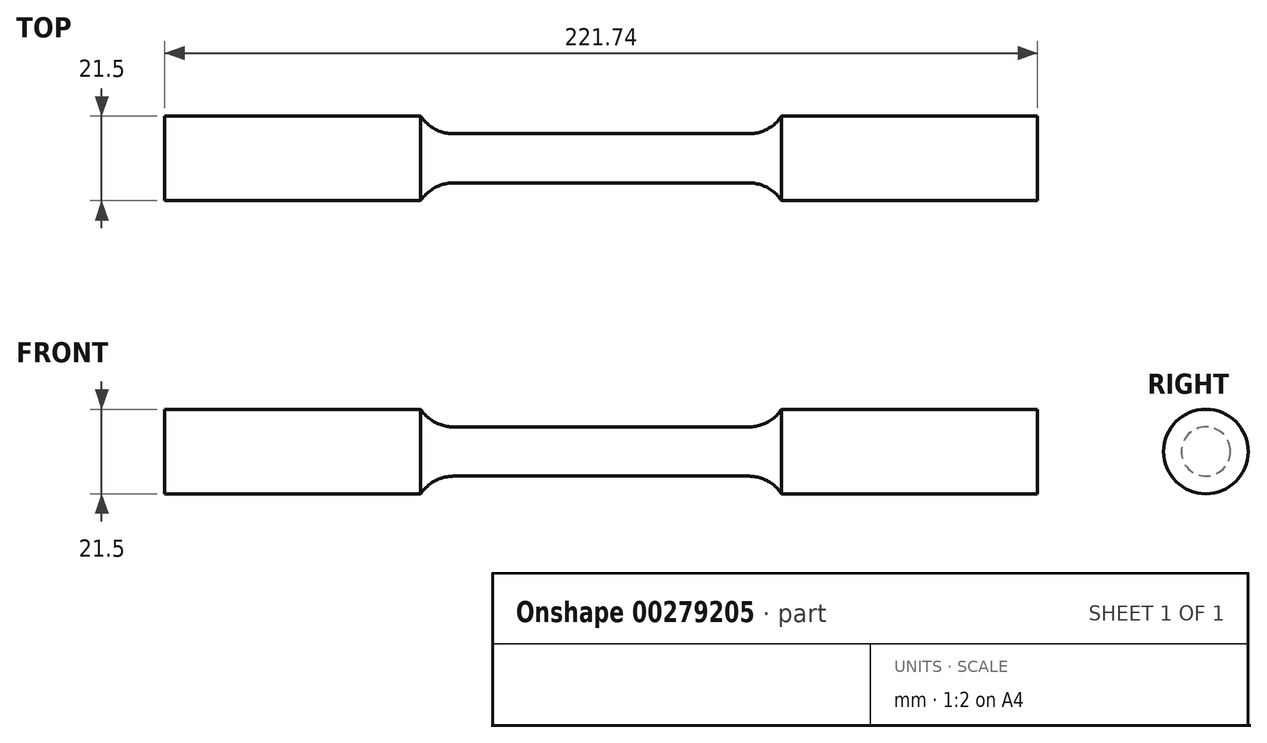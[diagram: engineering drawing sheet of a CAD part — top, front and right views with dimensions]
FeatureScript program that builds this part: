
annotation { "Feature Type Name" : "Feature", "Feature Type Description" : "" }
export const myFeature = defineFeature(function(context is Context, id is Id, definition is map)
    precondition{}
    {
        {
            var Q0;
            Q0=qCreatedBy(makeId("Front.planeOp"),FACE);
            var sketch = newSketch(context, id + "F0", { "sketchPlane" : qUnion([Q0])});
            skLineSegment(sketch, "E0", {"start": v(0, 6.25) * mm, "end": v(37.5, 6.25) * mm});
            skArc(sketch, "E1", {"start": v(37.5, 6.25) * mm, "mid": v(42.24, 7.45) * mm, "end": v(45.85, 10.75) * mm});
            skLineSegment(sketch, "E2", {"start": v(45.85, 10.75) * mm, "end": v(110.87, 10.75) * mm});
            skLineSegment(sketch, "E3", {"start": v(110.87, 10.75) * mm, "end": v(110.87, 0) * mm});
            skArc(sketch, "E4.MirrorCS", {"start": v(-37.5, 6.25) * mm, "mid": v(-42.24, 7.45) * mm, "end": v(-45.85, 10.75) * mm});
            skLineSegment(sketch, "E5.MirrorCS", {"start": v(0, 6.25) * mm, "end": v(-37.5, 6.25) * mm});
            skLineSegment(sketch, "E6.MirrorCS", {"start": v(-110.87, 10.75) * mm, "end": v(-110.87, 0) * mm});
            skLineSegment(sketch, "E7.MirrorCS", {"start": v(-45.85, 10.75) * mm, "end": v(-110.87, 10.75) * mm});
            skLineSegment(sketch, "E8", {"start": v(-110.87, 0) * mm, "end": v(110.87, 0) * mm});
            skSolve(sketch);
        }
        {
            var Q0;
            Q0 = qSketchRegion(id + "F0", true);
            var Q1;
            Q1=sQuery(id+"F0.wireOp",EDGE,"E8");
            revolve(context, id + "F1", {"entities" : qUnion([Q0]), "axis" : qUnion([Q1]), "revolveType" : RevolveType.FULL});
        }
    });
